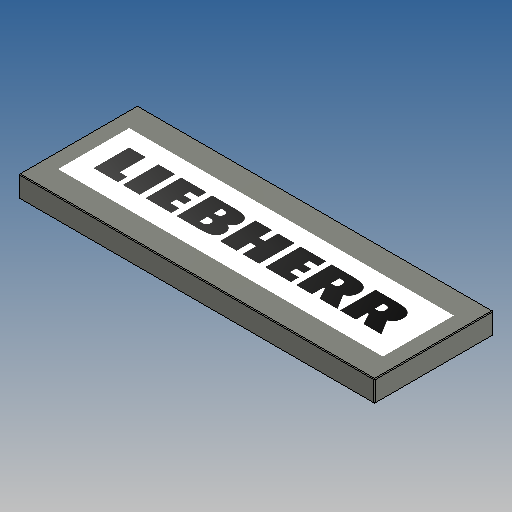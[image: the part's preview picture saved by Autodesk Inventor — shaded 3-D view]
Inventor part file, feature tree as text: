
AUTODESK INVENTOR PART (.ipt)
format: ipt  version: 2025 (Build 290162010, 162A)  size: 207,872 bytes
history: native  units: in
note: dims shown in document units (in); Inventor stores cm internally (conversion verified against a paired STEP export)
features: other x6, extrude x4, sketch x3, pattern_linear x1, fillet x1
ambient origin geometry x8: Origin, YZ Plane, XZ Plane, XY Plane, X Axis, Y Axis, Z Axis, Center Point
bodies: Solid1 (feature_tree)
feature tree (15):
  extrude  "Extrusion1"  Depth=0.6299in
  sketch  "Sketch3"  dims[d4=0.126in d5=0.0in d7=0.0591in d11=0.063in d12=0.0in]
  extrude  "Extrusion2"  Depth=0.063in TaperAngle=0.0deg
  extrude  "Extrusion7"  Depth=0.126in
  extrude  "Extrusion6"  Depth=0.315in
  pattern_linear  "Rectangular Pattern3"  Spacing1=0.315in  [1 undecoded]
  fillet  "Fillet1"  Radius=0.126in
  other  "Work Axis1"
  other  "Work Axis2"
  other  "Work Axis3"
  other  "Work Axis4"
  other  "Aufkleber1"
  sketch  "Sketch2"  dims[d0=1.8898in d1=0.6299in]
  sketch  "Skizze10"  dims[d22=0.0039in d61=0.189in d75=0.315in d76=0.315in d86=0.126in d87=0.0709in d88=0.0in d89=1.9685in d91=0.315in d92=0.315in d93=0.0in d94=0.0in d95=0.0in d96=0.0in d97=0.0in d98=1.5748in d99=0.315in d100=0.0in d101=0.0in d102=0.0157in d103=0.0157in d104=0.0157in d105=0.0in d107=0.126in d110=0.126in]
  other  "Bild1"
note: 1 required parameter value undecoded (feature->parameter linkage not recoverable at this tier; creation-order binding heuristic only, values carry confidence <= 0.55)
